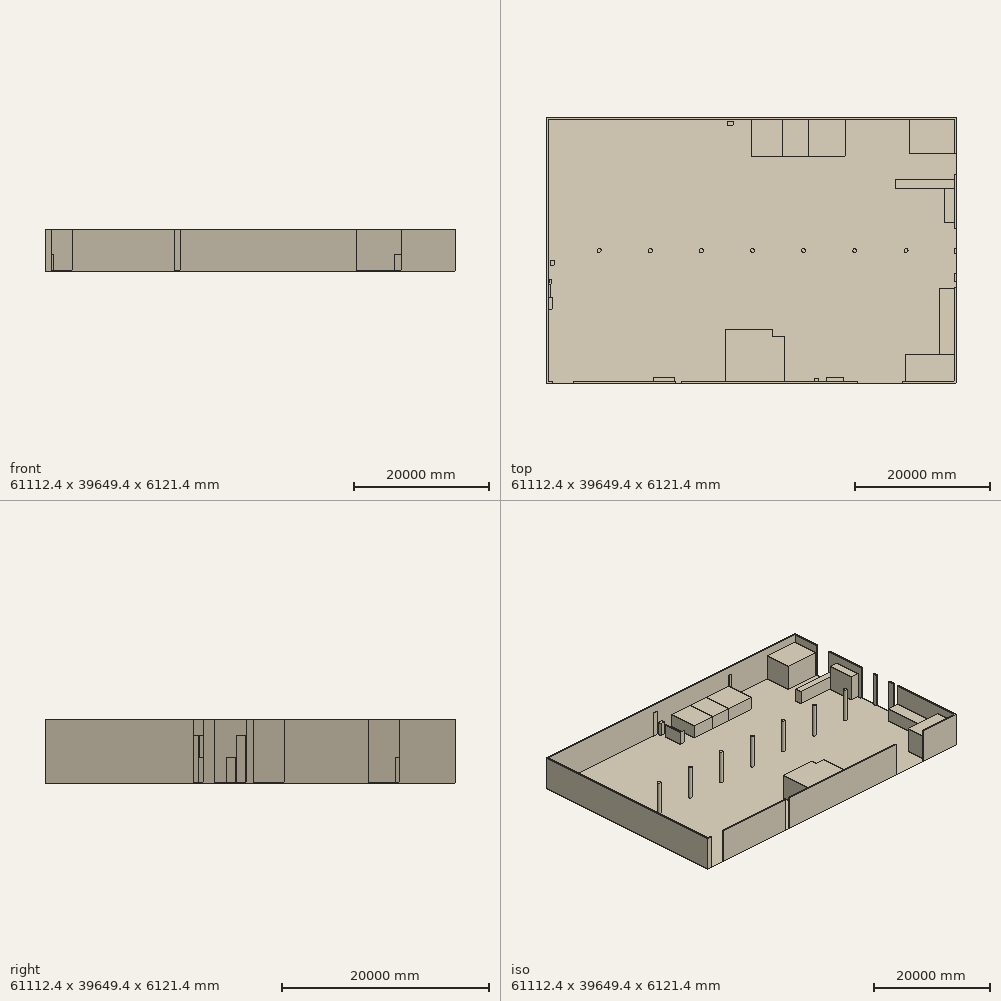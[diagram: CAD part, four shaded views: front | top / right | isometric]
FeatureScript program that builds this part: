
annotation { "Feature Type Name" : "Feature", "Feature Type Description" : "" }
export const myFeature = defineFeature(function(context is Context, id is Id, definition is map)
    precondition{}
    {
        {
            var Q0;
            Q0=qCreatedBy(makeId("Top.planeOp"),FACE);
            var sketch = newSketch(context, id + "F0", { "sketchPlane" : qUnion([Q0])});
            skLineSegment(sketch, "E0.bottom", {"start": v(30556.2, 19824.7) * mm, "end": v(-30556.2, 19824.7) * mm});
            skLineSegment(sketch, "E0.top", {"start": v(30556.2, -19824.7) * mm, "end": v(22479, -19824.7) * mm});
            skLineSegment(sketch, "E0.left", {"start": v(30556.2, 19824.7) * mm, "end": v(30556.2, 14439.9) * mm});
            skLineSegment(sketch, "E0.right", {"start": v(-30556.2, 19824.7) * mm, "end": v(-30556.2, -19824.7) * mm});
            skPoint(sketch, "E0.middle", {"position": v(0, 0) * mm});
            skPoint(sketch, "E1", {"position": v(30556.2, 18148.3) * mm});
            skPoint(sketch, "E2", {"position": v(30556.2, 15100.3) * mm});
            skPoint(sketch, "E3", {"position": v(30556.2, 14439.9) * mm});
            skPoint(sketch, "E4", {"position": v(30556.2, 11391.9) * mm});
            skPoint(sketch, "E5", {"position": v(30556.2, 10731.5) * mm});
            skPoint(sketch, "E6", {"position": v(30556.2, 7683.5) * mm});
            skPoint(sketch, "E7", {"position": v(30556.2, 7023.1) * mm});
            skPoint(sketch, "E8", {"position": v(30556.2, 3975.1) * mm});
            skPoint(sketch, "E9", {"position": v(30556.2, 3314.7) * mm});
            skPoint(sketch, "E10", {"position": v(30556.2, 266.7) * mm});
            skPoint(sketch, "E11", {"position": v(30556.2, -393.7) * mm});
            skPoint(sketch, "E12", {"position": v(30556.2, -3441.7) * mm});
            skPoint(sketch, "E13", {"position": v(30556.2, -4584.7) * mm});
            skPoint(sketch, "E14", {"position": v(30556.2, -5499.1) * mm});
            skPoint(sketch, "E15", {"position": v(-29641.8, -19824.7) * mm});
            skPoint(sketch, "E16", {"position": v(-26593.8, -19824.7) * mm});
            skPoint(sketch, "E17", {"position": v(-11353.8, -19824.7) * mm});
            skPoint(sketch, "E18", {"position": v(-10439.4, -19824.7) * mm});
            skPoint(sketch, "E19", {"position": v(15773.4, -19824.7) * mm});
            skPoint(sketch, "E20", {"position": v(22479, -19824.7) * mm});
            skLineSegment(sketch, "E21.0", {"start": v(30302.2, -19570.7) * mm, "end": v(22479, -19570.7) * mm});
            skLineSegment(sketch, "E21.1", {"start": v(30302.2, 19570.7) * mm, "end": v(30302.2, 14439.9) * mm});
            skLineSegment(sketch, "E21.2", {"start": v(30302.2, 19570.7) * mm, "end": v(-30302.2, 19570.7) * mm});
            skLineSegment(sketch, "E21.3", {"start": v(-30302.2, 19570.7) * mm, "end": v(-30302.2, -19570.7) * mm});
            skLineSegment(sketch, "E22", {"start": v(30556.2, 18148.3) * mm, "end": v(30302.2, 18148.3) * mm});
            skLineSegment(sketch, "E23", {"start": v(30556.2, 15100.3) * mm, "end": v(30302.2, 15100.3) * mm});
            skLineSegment(sketch, "E24", {"start": v(30556.2, 14439.9) * mm, "end": v(30302.2, 14439.9) * mm});
            skLineSegment(sketch, "E25", {"start": v(30556.2, 11391.9) * mm, "end": v(30302.2, 11391.9) * mm});
            skLineSegment(sketch, "E26", {"start": v(30556.2, 10731.5) * mm, "end": v(30302.2, 10731.5) * mm});
            skLineSegment(sketch, "E27", {"start": v(30556.2, 7683.5) * mm, "end": v(30302.2, 7683.5) * mm});
            skLineSegment(sketch, "E28", {"start": v(30556.2, 7023.1) * mm, "end": v(30302.2, 7023.1) * mm});
            skLineSegment(sketch, "E29", {"start": v(30556.2, 3975.1) * mm, "end": v(30302.2, 3975.1) * mm});
            skLineSegment(sketch, "E30", {"start": v(30556.2, 3314.7) * mm, "end": v(30302.2, 3314.7) * mm});
            skLineSegment(sketch, "E31", {"start": v(30556.2, 266.7) * mm, "end": v(30302.2, 266.7) * mm});
            skLineSegment(sketch, "E32", {"start": v(30556.2, -393.7) * mm, "end": v(30302.2, -393.7) * mm});
            skLineSegment(sketch, "E33", {"start": v(30556.2, -3441.7) * mm, "end": v(30302.2, -3441.7) * mm});
            skLineSegment(sketch, "E34", {"start": v(30556.2, -4584.7) * mm, "end": v(30302.2, -4584.7) * mm});
            skLineSegment(sketch, "E35", {"start": v(30556.2, -5499.1) * mm, "end": v(30302.2, -5499.1) * mm});
            skLineSegment(sketch, "E36", {"start": v(22479, -19824.7) * mm, "end": v(22479, -19570.7) * mm});
            skLineSegment(sketch, "E37", {"start": v(15773.4, -19824.7) * mm, "end": v(15773.4, -19570.7) * mm});
            skLineSegment(sketch, "E38", {"start": v(-10439.4, -19824.7) * mm, "end": v(-10439.4, -19570.7) * mm});
            skLineSegment(sketch, "E39", {"start": v(-11353.8, -19824.7) * mm, "end": v(-11353.8, -19570.7) * mm});
            skLineSegment(sketch, "E40", {"start": v(-26593.8, -19824.7) * mm, "end": v(-26593.8, -19570.7) * mm});
            skLineSegment(sketch, "E41", {"start": v(-29641.8, -19824.7) * mm, "end": v(-29641.8, -19570.7) * mm});
            skLineSegment(sketch, "E42.trimOffspring", {"start": v(-29641.8, -19824.7) * mm, "end": v(-30556.2, -19824.7) * mm});
            skLineSegment(sketch, "E43.trimOffspring", {"start": v(-29641.8, -19570.7) * mm, "end": v(-30302.2, -19570.7) * mm});
            skLineSegment(sketch, "E44.trimOffspring", {"start": v(-11353.8, -19824.7) * mm, "end": v(-26593.8, -19824.7) * mm});
            skLineSegment(sketch, "E45.trimOffspring", {"start": v(-11353.8, -19570.7) * mm, "end": v(-26593.8, -19570.7) * mm});
            skLineSegment(sketch, "E46.trimOffspring", {"start": v(15773.4, -19824.7) * mm, "end": v(-10439.4, -19824.7) * mm});
            skLineSegment(sketch, "E47.trimOffspring", {"start": v(15773.4, -19570.7) * mm, "end": v(-10439.4, -19570.7) * mm});
            skLineSegment(sketch, "E48.trimOffspring", {"start": v(30556.2, -5499.1) * mm, "end": v(30556.2, -19824.7) * mm});
            skLineSegment(sketch, "E49.trimOffspring", {"start": v(30302.2, -5499.1) * mm, "end": v(30302.2, -19570.7) * mm});
            skLineSegment(sketch, "E50.trimOffspring", {"start": v(30556.2, -3441.7) * mm, "end": v(30556.2, -4584.7) * mm});
            skLineSegment(sketch, "E51.trimOffspring", {"start": v(30302.2, -3441.7) * mm, "end": v(30302.2, -4584.7) * mm});
            skLineSegment(sketch, "E52.trimOffspring", {"start": v(30556.2, 266.7) * mm, "end": v(30556.2, -393.7) * mm});
            skLineSegment(sketch, "E53.trimOffspring", {"start": v(30302.2, 266.7) * mm, "end": v(30302.2, -393.7) * mm});
            skLineSegment(sketch, "E54.trimOffspring", {"start": v(30556.2, 11391.9) * mm, "end": v(30556.2, 3314.7) * mm});
            skLineSegment(sketch, "E55.trimOffspring", {"start": v(30302.2, 11391.9) * mm, "end": v(30302.2, 3314.7) * mm});
            skLineSegment(sketch, "E56", {"start": v(32965.05, -38.1) * mm, "end": v(-36390.89, -38.1) * mm, "construction": true});
            skPoint(sketch, "E57", {"position": v(23037.8, -38.1) * mm});
            skPoint(sketch, "E58", {"position": v(15417.8, -38.1) * mm});
            skPoint(sketch, "E59", {"position": v(7797.8, -38.1) * mm});
            skPoint(sketch, "E60", {"position": v(177.8, -38.1) * mm});
            skPoint(sketch, "E61", {"position": v(-7442.2, -38.1) * mm});
            skPoint(sketch, "E62", {"position": v(-15062.2, -38.1) * mm});
            skPoint(sketch, "E63", {"position": v(-22682.2, -38.1) * mm});
            skCircle(sketch, "E64", {"center": v(23037.8, -38.1) * mm, "radius": 304.8 * mm});
            skCircle(sketch, "E65", {"center": v(15417.8, -38.1) * mm, "radius": 304.8 * mm});
            skCircle(sketch, "E66", {"center": v(7797.8, -38.1) * mm, "radius": 304.8 * mm});
            skCircle(sketch, "E67", {"center": v(-7442.2, -38.1) * mm, "radius": 304.8 * mm});
            skCircle(sketch, "E68", {"center": v(-15062.2, -38.1) * mm, "radius": 304.8 * mm});
            skCircle(sketch, "E69", {"center": v(-22682.2, -38.1) * mm, "radius": 304.8 * mm});
            skCircle(sketch, "E70", {"center": v(177.8, -38.1) * mm, "radius": 304.8 * mm});
            skSolve(sketch);
        }
        {
            var Q0;
            {var subQ4=sQuery(id+"F0.wireOp",EDGE,"E0.bottom");Q0=makeQuery(id+"F0.imprint","IMPRINT",FACE,{"disambiguationData":[TD([[makeQuery(id+"F0.imprint","IMPRINT",EDGE,{"derivedFrom":subQ4}),1.0]])]});}
            var Q1;
            {var subQ0=sQuery(id+"F0.wireOp",EDGE,"E22");Q1=makeQuery(id+"F0.imprint","IMPRINT",FACE,{"disambiguationData":[TD([[makeQuery(id+"F0.imprint","IMPRINT",EDGE,{"derivedFrom":subQ0}),1.0]])]});}
            var Q2;
            {var subQ2=sQuery(id+"F0.wireOp",EDGE,"E23");Q2=makeQuery(id+"F0.imprint","IMPRINT",FACE,{"disambiguationData":[TD([[makeQuery(id+"F0.imprint","IMPRINT",EDGE,{"derivedFrom":subQ2}),1.0]])]});}
            var Q3;
            {var subQ0=sQuery(id+"F0.wireOp",EDGE,"E25");Q3=makeQuery(id+"F0.imprint","IMPRINT",FACE,{"disambiguationData":[TD([[makeQuery(id+"F0.imprint","IMPRINT",EDGE,{"derivedFrom":subQ0}),1.0]])]});}
            var Q4;
            {var subQ0=sQuery(id+"F0.wireOp",EDGE,"E26");Q4=makeQuery(id+"F0.imprint","IMPRINT",FACE,{"disambiguationData":[TD([[makeQuery(id+"F0.imprint","IMPRINT",EDGE,{"derivedFrom":subQ0}),1.0]])]});}
            var Q5;
            {var subQ0=sQuery(id+"F0.wireOp",EDGE,"E27");Q5=makeQuery(id+"F0.imprint","IMPRINT",FACE,{"disambiguationData":[TD([[makeQuery(id+"F0.imprint","IMPRINT",EDGE,{"derivedFrom":subQ0}),1.0]])]});}
            var Q6;
            {var subQ0=sQuery(id+"F0.wireOp",EDGE,"E28");Q6=makeQuery(id+"F0.imprint","IMPRINT",FACE,{"disambiguationData":[TD([[makeQuery(id+"F0.imprint","IMPRINT",EDGE,{"derivedFrom":subQ0}),1.0]])]});}
            var Q7;
            {var subQ0=sQuery(id+"F0.wireOp",EDGE,"E29");Q7=makeQuery(id+"F0.imprint","IMPRINT",FACE,{"disambiguationData":[TD([[makeQuery(id+"F0.imprint","IMPRINT",EDGE,{"derivedFrom":subQ0}),1.0]])]});}
            var Q8;
            Q8=makeQuery(id+"F0.imprint","IMPRINT",FACE,{"disambiguationData":[TD([[makeQuery(id+"F0.imprint","IMPRINT",EDGE,{"derivedFrom":sQuery(id+"F0.wireOp",EDGE,"E31")}),1.0]])]});
            var Q9;
            Q9=makeQuery(id+"F0.imprint","IMPRINT",FACE,{"disambiguationData":[TD([[makeQuery(id+"F0.imprint","IMPRINT",EDGE,{"derivedFrom":sQuery(id+"F0.wireOp",EDGE,"E33")}),1.0]])]});
            var Q10;
            Q10=makeQuery(id+"F0.imprint","IMPRINT",FACE,{"disambiguationData":[TD([[makeQuery(id+"F0.imprint","IMPRINT",EDGE,{"derivedFrom":sQuery(id+"F0.wireOp",EDGE,"E0.top")}),-1.0]])]});
            var Q11;
            Q11=makeQuery(id+"F0.imprint","IMPRINT",FACE,{"disambiguationData":[TD([[makeQuery(id+"F0.imprint","IMPRINT",EDGE,{"derivedFrom":sQuery(id+"F0.wireOp",EDGE,"E37")}),1.0]])]});
            var Q12;
            Q12=makeQuery(id+"F0.imprint","IMPRINT",FACE,{"disambiguationData":[TD([[makeQuery(id+"F0.imprint","IMPRINT",EDGE,{"derivedFrom":sQuery(id+"F0.wireOp",EDGE,"E39")}),1.0]])]});
            var Q13;
            Q13=makeQuery(id+"F0.imprint","IMPRINT",FACE,{"disambiguationData":[TD([[makeQuery(id+"F0.imprint","IMPRINT",EDGE,{"derivedFrom":sQuery(id+"F0.wireOp",EDGE,"E64")}),1.0]])]});
            var Q14;
            Q14=makeQuery(id+"F0.imprint","IMPRINT",FACE,{"disambiguationData":[TD([[makeQuery(id+"F0.imprint","IMPRINT",EDGE,{"derivedFrom":sQuery(id+"F0.wireOp",EDGE,"E65")}),1.0]])]});
            var Q15;
            Q15=makeQuery(id+"F0.imprint","IMPRINT",FACE,{"disambiguationData":[TD([[makeQuery(id+"F0.imprint","IMPRINT",EDGE,{"derivedFrom":sQuery(id+"F0.wireOp",EDGE,"E66")}),1.0]])]});
            var Q16;
            Q16=makeQuery(id+"F0.imprint","IMPRINT",FACE,{"disambiguationData":[TD([[makeQuery(id+"F0.imprint","IMPRINT",EDGE,{"derivedFrom":sQuery(id+"F0.wireOp",EDGE,"E67")}),1.0]])]});
            var Q17;
            Q17=makeQuery(id+"F0.imprint","IMPRINT",FACE,{"disambiguationData":[TD([[makeQuery(id+"F0.imprint","IMPRINT",EDGE,{"derivedFrom":sQuery(id+"F0.wireOp",EDGE,"E68")}),1.0]])]});
            var Q18;
            Q18=makeQuery(id+"F0.imprint","IMPRINT",FACE,{"disambiguationData":[TD([[makeQuery(id+"F0.imprint","IMPRINT",EDGE,{"derivedFrom":sQuery(id+"F0.wireOp",EDGE,"E69")}),1.0]])]});
            var Q19;
            Q19=makeQuery(id+"F0.imprint","IMPRINT",FACE,{"disambiguationData":[TD([[makeQuery(id+"F0.imprint","IMPRINT",EDGE,{"derivedFrom":sQuery(id+"F0.wireOp",EDGE,"E70")}),1.0]])]});
            extrude(context, id + "F1", {"entities" : qUnion([Q0, Q1, Q2, Q3, Q4, Q5, Q6, Q7, Q8, Q9, Q10, Q11, Q12, Q13, Q14, Q15, Q16, Q17, Q18, Q19]), "depth" : 6096 * mm, "offsetDistance" : 25.4 * mm});
        }
        {
            var Q0;
            Q0=qCreatedBy(makeId("Top.planeOp"),FACE);
            var sketch = newSketch(context, id + "F2", { "sketchPlane" : qUnion([Q0])});
            skLineSegment(sketch, "E71.0.0", {"start": v(30556.2, -5499.1) * mm, "end": v(30302.2, -5499.1) * mm, "construction": true});
            skLineSegment(sketch, "E71.0.1", {"start": v(30302.2, -5499.1) * mm, "end": v(30302.2, -19570.7) * mm, "construction": true});
            skLineSegment(sketch, "E71.0.2", {"start": v(30302.2, -19570.7) * mm, "end": v(22479, -19570.7) * mm, "construction": true});
            skLineSegment(sketch, "E71.0.3", {"start": v(22479, -19570.7) * mm, "end": v(22479, -19824.7) * mm, "construction": true});
            skLineSegment(sketch, "E71.0.4", {"start": v(22479, -19824.7) * mm, "end": v(30556.2, -19824.7) * mm, "construction": true});
            skLineSegment(sketch, "E71.0.5", {"start": v(30556.2, -19824.7) * mm, "end": v(30556.2, -5499.1) * mm, "construction": true});
            skLineSegment(sketch, "E72.0.0", {"start": v(-10439.4, -19570.7) * mm, "end": v(-10439.4, -19824.7) * mm, "construction": true});
            skLineSegment(sketch, "E72.0.1", {"start": v(-10439.4, -19824.7) * mm, "end": v(15773.4, -19824.7) * mm, "construction": true});
            skLineSegment(sketch, "E72.0.2", {"start": v(15773.4, -19824.7) * mm, "end": v(15773.4, -19570.7) * mm, "construction": true});
            skLineSegment(sketch, "E72.0.3", {"start": v(15773.4, -19570.7) * mm, "end": v(-10439.4, -19570.7) * mm, "construction": true});
            skLineSegment(sketch, "E73.0.0", {"start": v(-26593.8, -19570.7) * mm, "end": v(-26593.8, -19824.7) * mm, "construction": true});
            skLineSegment(sketch, "E73.0.1", {"start": v(-26593.8, -19824.7) * mm, "end": v(-11353.8, -19824.7) * mm, "construction": true});
            skLineSegment(sketch, "E73.0.2", {"start": v(-11353.8, -19824.7) * mm, "end": v(-11353.8, -19570.7) * mm, "construction": true});
            skLineSegment(sketch, "E73.0.3", {"start": v(-11353.8, -19570.7) * mm, "end": v(-26593.8, -19570.7) * mm, "construction": true});
            skLineSegment(sketch, "E74.0.0", {"start": v(-30302.2, 19570.7) * mm, "end": v(4546.6, 19570.7) * mm, "construction": true});
            skLineSegment(sketch, "E74.0.1", {"start": v(30302.2, 19570.7) * mm, "end": v(30302.2, 14439.9) * mm, "construction": true});
            skLineSegment(sketch, "E74.0.2", {"start": v(30302.2, 14439.9) * mm, "end": v(30556.2, 14439.9) * mm, "construction": true});
            skLineSegment(sketch, "E74.0.3", {"start": v(30556.2, 14439.9) * mm, "end": v(30556.2, 19824.7) * mm, "construction": true});
            skLineSegment(sketch, "E74.0.4", {"start": v(30556.2, 19824.7) * mm, "end": v(-30556.2, 19824.7) * mm, "construction": true});
            skLineSegment(sketch, "E74.0.5", {"start": v(-30556.2, 19824.7) * mm, "end": v(-30556.2, -19824.7) * mm, "construction": true});
            skLineSegment(sketch, "E74.0.6", {"start": v(-30556.2, -19824.7) * mm, "end": v(-29641.8, -19824.7) * mm, "construction": true});
            skLineSegment(sketch, "E74.0.7", {"start": v(-29641.8, -19824.7) * mm, "end": v(-29641.8, -19570.7) * mm, "construction": true});
            skLineSegment(sketch, "E74.0.8", {"start": v(-29641.8, -19570.7) * mm, "end": v(-30302.2, -19570.7) * mm, "construction": true});
            skLineSegment(sketch, "E74.0.9", {"start": v(-30302.2, -19570.7) * mm, "end": v(-30302.2, 19570.7) * mm, "construction": true});
            skLineSegment(sketch, "E75.0.0", {"start": v(30302.2, 11391.9) * mm, "end": v(30302.2, 3314.7) * mm, "construction": true});
            skLineSegment(sketch, "E75.0.1", {"start": v(30302.2, 3314.7) * mm, "end": v(30556.2, 3314.7) * mm, "construction": true});
            skLineSegment(sketch, "E75.0.2", {"start": v(30556.2, 3314.7) * mm, "end": v(30556.2, 11391.9) * mm, "construction": true});
            skLineSegment(sketch, "E75.0.3", {"start": v(30556.2, 11391.9) * mm, "end": v(30302.2, 11391.9) * mm, "construction": true});
            skLineSegment(sketch, "E76.0.0", {"start": v(30302.2, -393.7) * mm, "end": v(30556.2, -393.7) * mm, "construction": true});
            skLineSegment(sketch, "E76.0.1", {"start": v(30556.2, -393.7) * mm, "end": v(30556.2, 266.7) * mm, "construction": true});
            skLineSegment(sketch, "E76.0.2", {"start": v(30556.2, 266.7) * mm, "end": v(30302.2, 266.7) * mm, "construction": true});
            skLineSegment(sketch, "E76.0.3", {"start": v(30302.2, 266.7) * mm, "end": v(30302.2, -393.7) * mm, "construction": true});
            skLineSegment(sketch, "E77.0.0", {"start": v(30302.2, -4584.7) * mm, "end": v(30556.2, -4584.7) * mm, "construction": true});
            skLineSegment(sketch, "E77.0.1", {"start": v(30556.2, -4584.7) * mm, "end": v(30556.2, -3441.7) * mm, "construction": true});
            skLineSegment(sketch, "E77.0.2", {"start": v(30556.2, -3441.7) * mm, "end": v(30302.2, -3441.7) * mm, "construction": true});
            skLineSegment(sketch, "E77.0.3", {"start": v(30302.2, -3441.7) * mm, "end": v(30302.2, -4584.7) * mm, "construction": true});
            skLineSegment(sketch, "E78.bottom", {"start": v(22987, -19570.7) * mm, "end": v(30302.2, -19570.7) * mm});
            skLineSegment(sketch, "E78.top", {"start": v(22987, -15506.7) * mm, "end": v(28041.6, -15506.7) * mm});
            skLineSegment(sketch, "E78.left", {"start": v(22987, -19570.7) * mm, "end": v(22987, -15506.7) * mm});
            skLineSegment(sketch, "E78.right", {"start": v(30302.2, -19570.7) * mm, "end": v(30302.2, -15506.7) * mm});
            skLineSegment(sketch, "E79.bottom", {"start": v(30302.2, -15506.7) * mm, "end": v(28041.6, -15506.7) * mm});
            skLineSegment(sketch, "E79.top", {"start": v(30302.2, -5600.7) * mm, "end": v(28041.6, -5600.7) * mm});
            skLineSegment(sketch, "E79.left", {"start": v(30302.2, -15506.7) * mm, "end": v(30302.2, -5600.7) * mm});
            skLineSegment(sketch, "E79.right", {"start": v(28041.6, -15506.7) * mm, "end": v(28041.6, -5600.7) * mm});
            skLineSegment(sketch, "E80.bottom", {"start": v(30302.2, 9309.1) * mm, "end": v(21513.8, 9309.1) * mm});
            skLineSegment(sketch, "E80.top", {"start": v(30302.2, 10579.1) * mm, "end": v(21513.8, 10579.1) * mm});
            skLineSegment(sketch, "E80.left", {"start": v(30302.2, 9309.1) * mm, "end": v(30302.2, 10579.1) * mm});
            skLineSegment(sketch, "E80.right", {"start": v(21513.8, 9309.1) * mm, "end": v(21513.8, 10579.1) * mm});
            skLineSegment(sketch, "E81.top", {"start": v(30302.2, 4127.5) * mm, "end": v(28702, 4127.5) * mm});
            skLineSegment(sketch, "E81.left", {"start": v(30302.2, 9309.1) * mm, "end": v(30302.2, 4127.5) * mm});
            skLineSegment(sketch, "E81.right", {"start": v(28702, 9309.1) * mm, "end": v(28702, 4127.5) * mm});
            skLineSegment(sketch, "E82.bottom", {"start": v(30302.2, 14465.3) * mm, "end": v(23520.4, 14465.3) * mm});
            skLineSegment(sketch, "E82.top", {"start": v(30302.2, 19570.7) * mm, "end": v(23520.4, 19570.7) * mm});
            skLineSegment(sketch, "E82.left", {"start": v(30302.2, 14465.3) * mm, "end": v(30302.2, 19570.7) * mm});
            skLineSegment(sketch, "E82.right", {"start": v(23520.4, 14465.3) * mm, "end": v(23520.4, 19570.7) * mm});
            skLineSegment(sketch, "E83.bottom", {"start": v(14541.5, -16675.1) * mm, "end": v(8445.5, -16675.1) * mm});
            skLineSegment(sketch, "E83.top", {"start": v(14541.5, -15252.7) * mm, "end": v(8445.5, -15252.7) * mm});
            skLineSegment(sketch, "E83.left", {"start": v(14541.5, -16675.1) * mm, "end": v(14541.5, -15252.7) * mm});
            skLineSegment(sketch, "E83.right", {"start": v(8445.5, -16675.1) * mm, "end": v(8445.5, -15252.7) * mm});
            skLineSegment(sketch, "E84.bottom", {"start": v(14084.3, -11290.3) * mm, "end": v(15430.5, -11290.3) * mm, "construction": true});
            skLineSegment(sketch, "E84.top", {"start": v(14084.3, -13728.7) * mm, "end": v(15430.5, -13728.7) * mm, "construction": true});
            skLineSegment(sketch, "E84.left", {"start": v(14084.3, -11290.3) * mm, "end": v(14084.3, -13728.7) * mm, "construction": true});
            skLineSegment(sketch, "E84.right", {"start": v(15430.5, -11290.3) * mm, "end": v(15430.5, -13728.7) * mm, "construction": true});
            skLineSegment(sketch, "E85.bottom", {"start": v(17018, -5676.9) * mm, "end": v(15798.8, -5676.9) * mm});
            skLineSegment(sketch, "E85.top", {"start": v(17018, -3136.9) * mm, "end": v(15798.8, -3136.9) * mm});
            skLineSegment(sketch, "E85.left", {"start": v(17018, -5676.9) * mm, "end": v(17018, -3136.9) * mm});
            skLineSegment(sketch, "E86.bottom", {"start": v(17018, -1257.3) * mm, "end": v(15798.8, -1257.3) * mm});
            skLineSegment(sketch, "E86.top", {"start": v(17018, 1282.7) * mm, "end": v(15798.8, 1282.7) * mm});
            skLineSegment(sketch, "E86.left", {"start": v(17018, -1257.3) * mm, "end": v(17018, 1282.7) * mm});
            skLineSegment(sketch, "E87.bottom", {"start": v(17018, 3162.3) * mm, "end": v(15798.8, 3162.3) * mm});
            skLineSegment(sketch, "E87.top", {"start": v(17018, 5702.3) * mm, "end": v(15798.8, 5702.3) * mm});
            skLineSegment(sketch, "E87.left", {"start": v(17018, 3162.3) * mm, "end": v(17018, 5702.3) * mm});
            skLineSegment(sketch, "E87.right", {"start": v(2895.6, 3162.3) * mm, "end": v(2895.6, 5702.3) * mm});
            skLineSegment(sketch, "E88.bottom", {"start": v(17018, 7581.9) * mm, "end": v(15798.8, 7581.9) * mm});
            skLineSegment(sketch, "E88.top", {"start": v(17018, 10121.9) * mm, "end": v(15798.8, 10121.9) * mm});
            skLineSegment(sketch, "E88.left", {"start": v(17018, 7581.9) * mm, "end": v(17018, 10121.9) * mm});
            skLineSegment(sketch, "E89.bottom", {"start": v(-18034, -10198.1) * mm, "end": v(-13055.6, -10198.1) * mm});
            skLineSegment(sketch, "E89.top", {"start": v(-18034, -12331.7) * mm, "end": v(-13055.6, -12331.7) * mm});
            skLineSegment(sketch, "E89.left", {"start": v(-18034, -10198.1) * mm, "end": v(-18034, -12331.7) * mm});
            skLineSegment(sketch, "E89.right", {"start": v(-13055.6, -10198.1) * mm, "end": v(-13055.6, -12331.7) * mm});
            skLineSegment(sketch, "E90.bottom", {"start": v(-26492.2, -19570.7) * mm, "end": v(-15773.4, -19570.7) * mm});
            skLineSegment(sketch, "E90.top", {"start": v(-26492.2, -17970.5) * mm, "end": v(-15773.4, -17970.5) * mm});
            skLineSegment(sketch, "E90.left", {"start": v(-26492.2, -19570.7) * mm, "end": v(-26492.2, -17970.5) * mm});
            skLineSegment(sketch, "E90.right", {"start": v(-15773.4, -19570.7) * mm, "end": v(-15773.4, -17970.5) * mm});
            skLineSegment(sketch, "E91.bottom", {"start": v(-30302.2, -16446.5) * mm, "end": v(-29362.4, -16446.5) * mm});
            skLineSegment(sketch, "E91.top", {"start": v(-30302.2, -10172.7) * mm, "end": v(-29362.4, -10172.7) * mm});
            skLineSegment(sketch, "E91.left", {"start": v(-30302.2, -16446.5) * mm, "end": v(-30302.2, -10172.7) * mm});
            skLineSegment(sketch, "E91.right", {"start": v(-29362.4, -16446.5) * mm, "end": v(-29362.4, -10172.7) * mm});
            skLineSegment(sketch, "E92.bottom", {"start": v(-28676.6, -5803.9) * mm, "end": v(-27432, -5803.9) * mm});
            skLineSegment(sketch, "E92.top", {"start": v(-28676.6, -2146.3) * mm, "end": v(-27432, -2146.3) * mm});
            skLineSegment(sketch, "E92.left", {"start": v(-28676.6, -5803.9) * mm, "end": v(-28676.6, -2146.3) * mm});
            skLineSegment(sketch, "E92.right", {"start": v(-27432, -5803.9) * mm, "end": v(-27432, -2146.3) * mm});
            skLineSegment(sketch, "E93.bottom", {"start": v(-29718, 19570.7) * mm, "end": v(-27889.2, 19570.7) * mm});
            skLineSegment(sketch, "E93.top", {"start": v(-29718, 18986.5) * mm, "end": v(-27889.2, 18986.5) * mm});
            skLineSegment(sketch, "E93.left", {"start": v(-29718, 19570.7) * mm, "end": v(-29718, 18986.5) * mm});
            skLineSegment(sketch, "E93.right", {"start": v(-27889.2, 19570.7) * mm, "end": v(-27889.2, 18986.5) * mm});
            skLineSegment(sketch, "E94.bottom", {"start": v(-30302.2, 17792.7) * mm, "end": v(-29591, 17792.7) * mm});
            skLineSegment(sketch, "E94.top", {"start": v(-30302.2, 8128) * mm, "end": v(-29591, 8128) * mm});
            skLineSegment(sketch, "E94.left", {"start": v(-30302.2, 17792.7) * mm, "end": v(-30302.2, 8128) * mm});
            skLineSegment(sketch, "E94.right", {"start": v(-29591, 17792.7) * mm, "end": v(-29591, 8128) * mm});
            skLineSegment(sketch, "E95.bottom", {"start": v(13970, 19570.7) * mm, "end": v(8458.2, 19570.7) * mm});
            skLineSegment(sketch, "E95.top", {"start": v(13970, 14058.9) * mm, "end": v(8483.6, 14058.9) * mm});
            skLineSegment(sketch, "E95.left", {"start": v(13970, 19570.7) * mm, "end": v(13970, 14058.9) * mm});
            skLineSegment(sketch, "E95.right", {"start": v(8458.2, 19570.7) * mm, "end": v(8458.2, 14058.9) * mm});
            skLineSegment(sketch, "E96.bottom", {"start": v(8458.2, 19570.7) * mm, "end": v(4546.6, 19570.7) * mm});
            skLineSegment(sketch, "E96.top", {"start": v(8458.2, 14058.9) * mm, "end": v(4572, 14058.9) * mm});
            skLineSegment(sketch, "E96.right", {"start": v(4546.6, 19570.7) * mm, "end": v(4546.6, 14058.9) * mm});
            skLineSegment(sketch, "E97.bottom", {"start": v(4546.6, 19570.7) * mm, "end": v(-25.4, 19570.7) * mm});
            skLineSegment(sketch, "E97.top", {"start": v(4546.6, 14058.9) * mm, "end": v(-25.4, 14058.9) * mm});
            skLineSegment(sketch, "E97.right", {"start": v(-25.4, 19570.7) * mm, "end": v(-25.4, 14058.9) * mm});
            skLineSegment(sketch, "E98.bottom", {"start": v(-11531.6, -19570.7) * mm, "end": v(-14579.6, -19570.7) * mm});
            skLineSegment(sketch, "E98.top", {"start": v(-11531.6, -18961.1) * mm, "end": v(-14579.6, -18961.1) * mm});
            skLineSegment(sketch, "E98.left", {"start": v(-11531.6, -19570.7) * mm, "end": v(-11531.6, -18961.1) * mm});
            skLineSegment(sketch, "E98.right", {"start": v(-14579.6, -19570.7) * mm, "end": v(-14579.6, -18961.1) * mm});
            skLineSegment(sketch, "E99.bottom", {"start": v(13690.6, -19570.7) * mm, "end": v(11125.2, -19570.7) * mm});
            skLineSegment(sketch, "E99.top", {"start": v(13690.6, -18961.1) * mm, "end": v(11125.2, -18961.1) * mm});
            skLineSegment(sketch, "E99.left", {"start": v(13690.6, -19570.7) * mm, "end": v(13690.6, -18961.1) * mm});
            skLineSegment(sketch, "E99.right", {"start": v(11125.2, -19570.7) * mm, "end": v(11125.2, -18961.1) * mm});
            skLineSegment(sketch, "E100.bottom", {"start": v(2895.6, 3162.3) * mm, "end": v(609.6, 3162.3) * mm});
            skLineSegment(sketch, "E100.top", {"start": v(2895.6, 5702.3) * mm, "end": v(609.6, 5702.3) * mm});
            skLineSegment(sketch, "E100.right", {"start": v(609.6, 3162.3) * mm, "end": v(609.6, 5702.3) * mm});
            skLineSegment(sketch, "E101.bottom", {"start": v(-30302.2, -6997.7) * mm, "end": v(-29895.8, -6997.7) * mm});
            skLineSegment(sketch, "E101.top", {"start": v(-30302.2, -5067.3) * mm, "end": v(-29895.8, -5067.3) * mm});
            skLineSegment(sketch, "E101.left", {"start": v(-30302.2, -6997.7) * mm, "end": v(-30302.2, -5067.3) * mm});
            skLineSegment(sketch, "E101.right", {"start": v(-29895.8, -6997.7) * mm, "end": v(-29895.8, -5067.3) * mm});
            skLineSegment(sketch, "E102.bottom", {"start": v(2616.2, -5981.7) * mm, "end": v(1397, -5981.7) * mm, "construction": true});
            skLineSegment(sketch, "E102.top", {"start": v(2616.2, -2324.1) * mm, "end": v(1397, -2324.1) * mm, "construction": true});
            skLineSegment(sketch, "E102.left", {"start": v(2616.2, -5981.7) * mm, "end": v(2616.2, -2324.1) * mm, "construction": true});
            skLineSegment(sketch, "E102.right", {"start": v(1397, -5981.7) * mm, "end": v(1397, -2324.1) * mm, "construction": true});
            skLineSegment(sketch, "E103.left", {"start": v(2895.6, 10121.9) * mm, "end": v(2895.6, 10121.9) * mm});
            skLineSegment(sketch, "E104.top", {"start": v(17018, 10934.7) * mm, "end": v(15798.8, 10934.7) * mm});
            skLineSegment(sketch, "E104.left", {"start": v(17018, 10147.3) * mm, "end": v(17018, 10934.7) * mm});
            skLineSegment(sketch, "E104.right", {"start": v(15798.8, 10147.3) * mm, "end": v(15798.8, 10934.7) * mm});
            skLineSegment(sketch, "E105.bottom", {"start": v(-30302.2, -10172.7) * mm, "end": v(-28778.2, -10172.7) * mm});
            skLineSegment(sketch, "E105.top", {"start": v(-30302.2, -9486.9) * mm, "end": v(-28778.2, -9486.9) * mm});
            skLineSegment(sketch, "E105.left", {"start": v(-30302.2, -10172.7) * mm, "end": v(-30302.2, -9486.9) * mm});
            skLineSegment(sketch, "E105.right", {"start": v(-28778.2, -10172.7) * mm, "end": v(-28778.2, -9486.9) * mm});
            skLineSegment(sketch, "E106", {"start": v(-29591, 13220.7) * mm, "end": v(-30302.2, 13220.7) * mm});
            skLineSegment(sketch, "E107.bottom", {"start": v(-26670, 19570.7) * mm, "end": v(-24841.2, 19570.7) * mm});
            skLineSegment(sketch, "E107.top", {"start": v(-26670, 18808.7) * mm, "end": v(-24841.2, 18808.7) * mm});
            skLineSegment(sketch, "E107.left", {"start": v(-26670, 19570.7) * mm, "end": v(-26670, 18808.7) * mm});
            skLineSegment(sketch, "E107.right", {"start": v(-24841.2, 19570.7) * mm, "end": v(-24841.2, 18808.7) * mm});
            skLineSegment(sketch, "E108.bottom", {"start": v(-30302.2, -6997.7) * mm, "end": v(-29641.8, -6997.7) * mm});
            skLineSegment(sketch, "E108.top", {"start": v(-30302.2, -8826.5) * mm, "end": v(-29641.8, -8826.5) * mm});
            skLineSegment(sketch, "E108.left", {"start": v(-30302.2, -6997.7) * mm, "end": v(-30302.2, -8826.5) * mm});
            skLineSegment(sketch, "E108.right", {"start": v(-29641.8, -6997.7) * mm, "end": v(-29641.8, -8826.5) * mm});
            skLineSegment(sketch, "E109.bottom", {"start": v(-30302.2, 6705.6) * mm, "end": v(-27254.2, 6705.6) * mm});
            skLineSegment(sketch, "E109.top", {"start": v(-30302.2, 5562.6) * mm, "end": v(-27254.2, 5562.6) * mm});
            skLineSegment(sketch, "E109.left", {"start": v(-30302.2, 6705.6) * mm, "end": v(-30302.2, 5562.6) * mm});
            skLineSegment(sketch, "E109.right", {"start": v(-27254.2, 6705.6) * mm, "end": v(-27254.2, 5562.6) * mm});
            skLineSegment(sketch, "E110.bottom", {"start": v(-29514.8, 5562.6) * mm, "end": v(-27990.8, 5562.6) * mm});
            skLineSegment(sketch, "E110.top", {"start": v(-29514.8, 5257.8) * mm, "end": v(-27990.8, 5257.8) * mm});
            skLineSegment(sketch, "E110.left", {"start": v(-29514.8, 5562.6) * mm, "end": v(-29514.8, 5257.8) * mm});
            skLineSegment(sketch, "E110.right", {"start": v(-27990.8, 5562.6) * mm, "end": v(-27990.8, 5257.8) * mm});
            skLineSegment(sketch, "E111.bottom", {"start": v(-27889.2, 19265.9) * mm, "end": v(-26670, 19265.9) * mm});
            skLineSegment(sketch, "E111.top", {"start": v(-27889.2, 19570.7) * mm, "end": v(-26670, 19570.7) * mm});
            skLineSegment(sketch, "E111.left", {"start": v(-27889.2, 19265.9) * mm, "end": v(-27889.2, 19570.7) * mm});
            skLineSegment(sketch, "E111.right", {"start": v(-26670, 19265.9) * mm, "end": v(-26670, 19570.7) * mm});
            skLineSegment(sketch, "E112.bottom", {"start": v(9982.2, -19570.7) * mm, "end": v(9321.8, -19570.7) * mm});
            skLineSegment(sketch, "E112.top", {"start": v(9982.2, -19151.6) * mm, "end": v(9321.8, -19151.6) * mm});
            skLineSegment(sketch, "E112.left", {"start": v(9982.2, -19570.7) * mm, "end": v(9982.2, -19151.6) * mm});
            skLineSegment(sketch, "E112.right", {"start": v(9321.8, -19570.7) * mm, "end": v(9321.8, -19151.6) * mm});
            skLineSegment(sketch, "E113.bottom", {"start": v(4940.3, -19570.7) * mm, "end": v(-3816.35, -19570.7) * mm});
            skLineSegment(sketch, "E113.top", {"start": v(3200.4, -11760.2) * mm, "end": v(-3816.35, -11760.2) * mm});
            skLineSegment(sketch, "E113.left", {"start": v(4940.3, -19570.7) * mm, "end": v(4940.3, -12776.2) * mm});
            skLineSegment(sketch, "E113.right", {"start": v(-3816.35, -19570.7) * mm, "end": v(-3816.35, -11760.2) * mm});
            skLineSegment(sketch, "E114.top", {"start": v(4940.3, -12776.2) * mm, "end": v(3200.4, -12776.2) * mm});
            skLineSegment(sketch, "E114.right", {"start": v(3200.4, -11760.2) * mm, "end": v(3200.4, -12776.2) * mm});
            skLineSegment(sketch, "E115", {"start": v(6121.4, -5676.9) * mm, "end": v(6121.4, -3136.9) * mm});
            skLineSegment(sketch, "E116.trimOffspring", {"start": v(6121.4, -1257.3) * mm, "end": v(6121.4, 1282.7) * mm});
            skLineSegment(sketch, "E117.right", {"start": v(-4832.35, -12420.6) * mm, "end": v(-4832.35, -18605.5) * mm});
            skLineSegment(sketch, "E118.bottom", {"start": v(-4832.35, -18605.5) * mm, "end": v(-10420.35, -18605.5) * mm});
            skLineSegment(sketch, "E118.top", {"start": v(-4832.35, -19570.7) * mm, "end": v(-10420.35, -19570.7) * mm});
            skLineSegment(sketch, "E118.left", {"start": v(-4832.35, -18605.5) * mm, "end": v(-4832.35, -19570.7) * mm});
            skLineSegment(sketch, "E118.right", {"start": v(-10420.35, -18605.5) * mm, "end": v(-10420.35, -19570.7) * mm});
            skLineSegment(sketch, "E119", {"start": v(-4832.35, -12420.6) * mm, "end": v(-3867.15, -12420.6) * mm});
            skLineSegment(sketch, "E120", {"start": v(-3867.15, -12420.6) * mm, "end": v(-3867.15, -18605.5) * mm});
            skLineSegment(sketch, "E121", {"start": v(-3867.15, -18605.5) * mm, "end": v(-4832.35, -18605.5) * mm});
            skLineSegment(sketch, "E122", {"start": v(8483.6, 19570.7) * mm, "end": v(8483.6, 14058.9) * mm});
            skLineSegment(sketch, "E123", {"start": v(4572, 19570.7) * mm, "end": v(4572, 14058.9) * mm});
            skLineSegment(sketch, "E124.trimOffspring", {"start": v(8483.6, 19570.7) * mm, "end": v(13970, 19570.7) * mm, "construction": true});
            skLineSegment(sketch, "E125.trimOffspring", {"start": v(4572, 19570.7) * mm, "end": v(8458.2, 19570.7) * mm, "construction": true});
            skLineSegment(sketch, "E126", {"start": v(2895.6, 7581.9) * mm, "end": v(1651, 7581.9) * mm});
            skLineSegment(sketch, "E127", {"start": v(1651, 7581.9) * mm, "end": v(1651, 8216.9) * mm});
            skLineSegment(sketch, "E128", {"start": v(1651, 8216.9) * mm, "end": v(2895.6, 8216.9) * mm});
            skLineSegment(sketch, "E129", {"start": v(2895.6, 8242.3) * mm, "end": v(2895.6, 10096.5) * mm});
            skLineSegment(sketch, "E130", {"start": v(2895.6, 10121.9) * mm, "end": v(2184.4, 10121.9) * mm});
            skLineSegment(sketch, "E131", {"start": v(2184.4, 10096.5) * mm, "end": v(2184.4, 8242.3) * mm});
            skLineSegment(sketch, "E132", {"start": v(2895.6, 10121.9) * mm, "end": v(2895.6, 11137.9) * mm});
            skLineSegment(sketch, "E133", {"start": v(2895.6, 11137.9) * mm, "end": v(1879.6, 11137.9) * mm});
            skLineSegment(sketch, "E134", {"start": v(1854.2, 11137.9) * mm, "end": v(1854.2, 10121.9) * mm});
            skLineSegment(sketch, "E135", {"start": v(1879.6, 10121.9) * mm, "end": v(2895.6, 10121.9) * mm});
            skLineSegment(sketch, "E136", {"start": v(1854.2, 11137.9) * mm, "end": v(838.2, 11137.9) * mm});
            skLineSegment(sketch, "E137", {"start": v(838.2, 11137.9) * mm, "end": v(838.2, 10121.9) * mm});
            skLineSegment(sketch, "E138", {"start": v(838.2, 10121.9) * mm, "end": v(1854.2, 10121.9) * mm});
            skLineSegment(sketch, "E139", {"start": v(15798.8, 10121.9) * mm, "end": v(15798.8, 7581.9) * mm});
            skLineSegment(sketch, "E140", {"start": v(15798.8, 10121.9) * mm, "end": v(15798.8, 10121.9) * mm});
            skLineSegment(sketch, "E141", {"start": v(15773.4, 9512.3) * mm, "end": v(2921, 9512.3) * mm});
            skLineSegment(sketch, "E142", {"start": v(15798.8, 5702.3) * mm, "end": v(15798.8, 3162.3) * mm});
            skLineSegment(sketch, "E143", {"start": v(15798.8, 1282.7) * mm, "end": v(15798.8, -1257.3) * mm});
            skLineSegment(sketch, "E144", {"start": v(15798.8, -3136.9) * mm, "end": v(15798.8, -5676.9) * mm});
            skLineSegment(sketch, "E145", {"start": v(1879.6, 11137.9) * mm, "end": v(1879.6, 10121.9) * mm});
            skLineSegment(sketch, "E146", {"start": v(2184.4, 10096.5) * mm, "end": v(2895.6, 10096.5) * mm});
            skLineSegment(sketch, "E147", {"start": v(2184.4, 8242.3) * mm, "end": v(2895.6, 8242.3) * mm});
            skLineSegment(sketch, "E148", {"start": v(2921, 9512.3) * mm, "end": v(2921, 7581.9) * mm});
            skLineSegment(sketch, "E149.trimOffspring", {"start": v(2895.6, 10096.5) * mm, "end": v(2895.6, 8242.3) * mm});
            skLineSegment(sketch, "E150.trimOffspring", {"start": v(2895.6, 8216.9) * mm, "end": v(2895.6, 7581.9) * mm});
            skLineSegment(sketch, "E151", {"start": v(15773.4, 9512.3) * mm, "end": v(15773.4, 7581.9) * mm});
            skLineSegment(sketch, "E152", {"start": v(15773.4, 5702.3) * mm, "end": v(15773.4, 3162.3) * mm});
            skLineSegment(sketch, "E153", {"start": v(15773.4, 1282.7) * mm, "end": v(15773.4, -1257.3) * mm});
            skLineSegment(sketch, "E154", {"start": v(15773.4, -3136.9) * mm, "end": v(15773.4, -5676.9) * mm});
            skLineSegment(sketch, "E155.trimOffspring", {"start": v(15773.4, -5676.9) * mm, "end": v(6121.4, -5676.9) * mm});
            skLineSegment(sketch, "E156.trimOffspring", {"start": v(15773.4, -3136.9) * mm, "end": v(6121.4, -3136.9) * mm});
            skLineSegment(sketch, "E157.trimOffspring", {"start": v(15773.4, -1257.3) * mm, "end": v(6121.4, -1257.3) * mm});
            skLineSegment(sketch, "E158.trimOffspring", {"start": v(15773.4, 1282.7) * mm, "end": v(6121.4, 1282.7) * mm});
            skLineSegment(sketch, "E159.trimOffspring", {"start": v(15773.4, 3162.3) * mm, "end": v(2895.6, 3162.3) * mm});
            skLineSegment(sketch, "E160.trimOffspring", {"start": v(15773.4, 5702.3) * mm, "end": v(2895.6, 5702.3) * mm});
            skLineSegment(sketch, "E161.trimOffspring", {"start": v(15773.4, 7581.9) * mm, "end": v(2921, 7581.9) * mm});
            skLineSegment(sketch, "E162", {"start": v(15798.8, 10147.3) * mm, "end": v(17018, 10147.3) * mm});
            skLineSegment(sketch, "E163.bottom", {"start": v(-812.8, 19024.6) * mm, "end": v(-127, 19024.6) * mm});
            skLineSegment(sketch, "E163.top", {"start": v(-812.8, 16560.8) * mm, "end": v(-127, 16560.8) * mm});
            skLineSegment(sketch, "E163.left", {"start": v(-812.8, 19024.6) * mm, "end": v(-812.8, 16560.8) * mm});
            skLineSegment(sketch, "E163.right", {"start": v(-127, 19024.6) * mm, "end": v(-127, 16560.8) * mm});
            skLineSegment(sketch, "E164.bottom", {"start": v(-977.9, 16535.4) * mm, "end": v(-127, 16535.4) * mm});
            skLineSegment(sketch, "E164.top", {"start": v(-977.9, 15011.4) * mm, "end": v(-127, 15011.4) * mm});
            skLineSegment(sketch, "E164.left", {"start": v(-977.9, 16535.4) * mm, "end": v(-977.9, 15011.4) * mm});
            skLineSegment(sketch, "E164.right", {"start": v(-127, 16535.4) * mm, "end": v(-127, 15011.4) * mm});
            skLineSegment(sketch, "E165.bottom", {"start": v(-3263.9, 17805.4) * mm, "end": v(-3225.8, 17805.4) * mm});
            skLineSegment(sketch, "E165.left", {"start": v(-3263.9, 17805.4) * mm, "end": v(-3263.9, 14147.8) * mm});
            skLineSegment(sketch, "E165.right", {"start": v(-3225.8, 17805.4) * mm, "end": v(-3225.8, 14185.9) * mm});
            skLineSegment(sketch, "E166", {"start": v(-2393.95, 14147.8) * mm, "end": v(-2393.95, 14185.9) * mm});
            skLineSegment(sketch, "E167", {"start": v(-2393.95, 14185.9) * mm, "end": v(-3225.8, 14185.9) * mm});
            skLineSegment(sketch, "E168", {"start": v(-3263.9, 14147.8) * mm, "end": v(-2393.95, 14147.8) * mm});
            skLineSegment(sketch, "E169.bottom", {"start": v(-3517.9, 19227.8) * mm, "end": v(-2717.8, 19227.8) * mm});
            skLineSegment(sketch, "E169.top", {"start": v(-3517.9, 18669) * mm, "end": v(-2717.8, 18669) * mm});
            skLineSegment(sketch, "E169.left", {"start": v(-3517.9, 19227.8) * mm, "end": v(-3517.9, 18669) * mm});
            skLineSegment(sketch, "E169.right", {"start": v(-2717.8, 19227.8) * mm, "end": v(-2717.8, 18669) * mm});
            skLineSegment(sketch, "E170.bottom", {"start": v(-3733.8, 19570.7) * mm, "end": v(-4559.3, 19570.7) * mm});
            skLineSegment(sketch, "E170.top", {"start": v(-3733.8, 19469.1) * mm, "end": v(-4559.3, 19469.1) * mm});
            skLineSegment(sketch, "E170.left", {"start": v(-3733.8, 19570.7) * mm, "end": v(-3733.8, 19469.1) * mm});
            skLineSegment(sketch, "E170.right", {"start": v(-4559.3, 19570.7) * mm, "end": v(-4559.3, 19469.1) * mm});
            skLineSegment(sketch, "E171.bottom", {"start": v(13970, 19570.7) * mm, "end": v(14490.7, 19570.7) * mm});
            skLineSegment(sketch, "E171.top", {"start": v(13982.7, 19469.1) * mm, "end": v(14490.7, 19469.1) * mm});
            skLineSegment(sketch, "E171.right", {"start": v(14490.7, 19570.7) * mm, "end": v(14490.7, 19469.1) * mm});
            skLineSegment(sketch, "E172", {"start": v(13982.7, 19469.1) * mm, "end": v(13982.7, 19570.7) * mm});
            skLineSegment(sketch, "E173.trimOffspring", {"start": v(13982.7, 19570.7) * mm, "end": v(30302.2, 19570.7) * mm, "construction": true});
            skLineSegment(sketch, "E174.bottom", {"start": v(-30302.2, -5041.9) * mm, "end": v(-29857.7, -5041.9) * mm});
            skLineSegment(sketch, "E174.top", {"start": v(-30302.2, -4381.5) * mm, "end": v(-29857.7, -4381.5) * mm});
            skLineSegment(sketch, "E174.left", {"start": v(-30302.2, -5041.9) * mm, "end": v(-30302.2, -4381.5) * mm});
            skLineSegment(sketch, "E174.right", {"start": v(-29857.7, -5041.9) * mm, "end": v(-29857.7, -4381.5) * mm});
            skLineSegment(sketch, "E175.bottom", {"start": v(-30302.2, -4965.7) * mm, "end": v(-30143.45, -4965.7) * mm});
            skLineSegment(sketch, "E175.top", {"start": v(-30302.2, -4419.6) * mm, "end": v(-30143.45, -4419.6) * mm});
            skLineSegment(sketch, "E175.left", {"start": v(-30302.2, -4965.7) * mm, "end": v(-30302.2, -4419.6) * mm});
            skLineSegment(sketch, "E175.right", {"start": v(-30143.45, -4965.7) * mm, "end": v(-30143.45, -4419.6) * mm});
            skLineSegment(sketch, "E176.bottom", {"start": v(-30302.2, -4127.5) * mm, "end": v(-30200.6, -4127.5) * mm});
            skLineSegment(sketch, "E176.top", {"start": v(-30302.2, -3733.8) * mm, "end": v(-30200.6, -3733.8) * mm});
            skLineSegment(sketch, "E176.left", {"start": v(-30302.2, -4127.5) * mm, "end": v(-30302.2, -3733.8) * mm});
            skLineSegment(sketch, "E176.right", {"start": v(-30200.6, -4127.5) * mm, "end": v(-30200.6, -3733.8) * mm});
            skLineSegment(sketch, "E177.bottom", {"start": v(-29959.3, -2298.7) * mm, "end": v(-29400.5, -2298.7) * mm});
            skLineSegment(sketch, "E177.top", {"start": v(-29959.3, -1498.6) * mm, "end": v(-29400.5, -1498.6) * mm});
            skLineSegment(sketch, "E177.left", {"start": v(-29959.3, -2298.7) * mm, "end": v(-29959.3, -1498.6) * mm});
            skLineSegment(sketch, "E177.right", {"start": v(-29400.5, -2298.7) * mm, "end": v(-29400.5, -1498.6) * mm});
            skLineSegment(sketch, "E178.bottom", {"start": v(-30302.2, -1333.5) * mm, "end": v(-30200.6, -1333.5) * mm});
            skLineSegment(sketch, "E178.top", {"start": v(-30302.2, -520.7) * mm, "end": v(-30200.6, -520.7) * mm});
            skLineSegment(sketch, "E178.left", {"start": v(-30302.2, -1333.5) * mm, "end": v(-30302.2, -520.7) * mm});
            skLineSegment(sketch, "E178.right", {"start": v(-30200.6, -1333.5) * mm, "end": v(-30200.6, -520.7) * mm});
            skLineSegment(sketch, "E179.bottom", {"start": v(-3213.1, 17805.4) * mm, "end": v(-2882.9, 17805.4) * mm});
            skLineSegment(sketch, "E179.top", {"start": v(-3213.1, 16586.2) * mm, "end": v(-2882.9, 16586.2) * mm});
            skLineSegment(sketch, "E179.left", {"start": v(-3213.1, 17805.4) * mm, "end": v(-3213.1, 16586.2) * mm});
            skLineSegment(sketch, "E179.right", {"start": v(-2882.9, 17805.4) * mm, "end": v(-2882.9, 16586.2) * mm});
            skSolve(sketch);
        }
        {
            var Q0;
            Q0=makeQuery(id+"F2.imprint","IMPRINT",FACE,{"disambiguationData":[TD([[makeQuery(id+"F2.imprint","IMPRINT",EDGE,{"derivedFrom":sQuery(id+"F2.wireOp",EDGE,"E101.top")}),-1.0]])]});
            var Q1;
            Q1=makeQuery(id+"F2.imprint","IMPRINT",FACE,{"disambiguationData":[TD([[makeQuery(id+"F2.imprint","IMPRINT",EDGE,{"derivedFrom":sQuery(id+"F2.wireOp",EDGE,"E98.bottom")}),-1.0]])]});
            var Q2;
            Q2=makeQuery(id+"F2.imprint","IMPRINT",FACE,{"disambiguationData":[TD([[makeQuery(id+"F2.imprint","IMPRINT",EDGE,{"derivedFrom":sQuery(id+"F2.wireOp",EDGE,"E99.bottom")}),-1.0]])]});
            var Q3;
            Q3=makeQuery(id+"F2.imprint","IMPRINT",FACE,{"disambiguationData":[TD([[makeQuery(id+"F2.imprint","IMPRINT",EDGE,{"derivedFrom":sQuery(id+"F2.wireOp",EDGE,"E84.bottom")}),-1.0]])]});
            var Q4;
            Q4=makeQuery(id+"F2.imprint","IMPRINT",FACE,{"disambiguationData":[TD([[makeQuery(id+"F2.imprint","IMPRINT",EDGE,{"derivedFrom":sQuery(id+"F2.wireOp",EDGE,"E78.bottom")}),1.0]])]});
            var Q5;
            Q5=makeQuery(id+"F2.imprint","IMPRINT",FACE,{"disambiguationData":[TD([[makeQuery(id+"F2.imprint","IMPRINT",EDGE,{"derivedFrom":sQuery(id+"F2.wireOp",EDGE,"E102.bottom")}),-1.0]])]});
            var Q6;
            Q6=makeQuery(id+"F2.imprint","IMPRINT",FACE,{"disambiguationData":[TD([[makeQuery(id+"F2.imprint","IMPRINT",EDGE,{"derivedFrom":sQuery(id+"F2.wireOp",EDGE,"E81.top")}),-1.0]])]});
            var Q7;
            Q7=makeQuery(id+"F2.imprint","IMPRINT",FACE,{"disambiguationData":[TD([[makeQuery(id+"F2.imprint","IMPRINT",EDGE,{"derivedFrom":sQuery(id+"F2.wireOp",EDGE,"E82.bottom")}),-1.0]])]});
            var Q8;
            Q8=makeQuery(id+"F2.imprint","IMPRINT",FACE,{"disambiguationData":[TD([[makeQuery(id+"F2.imprint","IMPRINT",EDGE,{"derivedFrom":sQuery(id+"F2.wireOp",EDGE,"E113.bottom")}),-1.0]])]});
            var Q9;
            Q9=makeQuery(id+"F2.imprint","IMPRINT",FACE,{"disambiguationData":[TD([[makeQuery(id+"F2.imprint","IMPRINT",EDGE,{"derivedFrom":sQuery(id+"F2.wireOp",EDGE,"E171.top")}),1.0]])]});
            var Q10;
            Q10=makeQuery(id+"F2.imprint","IMPRINT",FACE,{"disambiguationData":[TD([[makeQuery(id+"F2.imprint","IMPRINT",EDGE,{"derivedFrom":sQuery(id+"F2.wireOp",EDGE,"E170.bottom")}),1.0]])]});
            var Q11;
            Q11=makeQuery(id+"F2.imprint","IMPRINT",FACE,{"disambiguationData":[TD([[makeQuery(id+"F2.imprint","IMPRINT",EDGE,{"derivedFrom":sQuery(id+"F2.wireOp",EDGE,"E175.bottom")}),1.0]])]});
            var Q12;
            Q12=makeQuery(id+"F2.imprint","IMPRINT",FACE,{"disambiguationData":[TD([[makeQuery(id+"F2.imprint","IMPRINT",EDGE,{"derivedFrom":sQuery(id+"F2.wireOp",EDGE,"E176.bottom")}),1.0]])]});
            var Q13;
            Q13=makeQuery(id+"F2.imprint","IMPRINT",FACE,{"disambiguationData":[TD([[makeQuery(id+"F2.imprint","IMPRINT",EDGE,{"derivedFrom":sQuery(id+"F2.wireOp",EDGE,"E178.bottom")}),1.0]])]});
            extrude(context, id + "F3", {"entities" : qUnion([Q0, Q1, Q2, Q3, Q4, Q5, Q6, Q7, Q8, Q9, Q10, Q11, Q12, Q13]), "flatOperationType" : FlatOperationType.REMOVE, "depth" : 4572 * mm, "offsetDistance" : 25.4 * mm, "domain" : OperationDomain.MODEL});
        }
        {
            var Q0;
            Q0=makeQuery(id+"F2.imprint","IMPRINT",FACE,{"disambiguationData":[TD([[makeQuery(id+"F2.imprint","IMPRINT",EDGE,{"derivedFrom":sQuery(id+"F2.wireOp",EDGE,"E108.top")}),1.0]])]});
            var Q1;
            Q1=makeQuery(id+"F2.imprint","IMPRINT",FACE,{"disambiguationData":[TD([[makeQuery(id+"F2.imprint","IMPRINT",EDGE,{"derivedFrom":sQuery(id+"F2.wireOp",EDGE,"E96.bottom")}),1.0]])]});
            var Q2;
            Q2=makeQuery(id+"F2.imprint","IMPRINT",FACE,{"disambiguationData":[TD([[makeQuery(id+"F2.imprint","IMPRINT",EDGE,{"derivedFrom":sQuery(id+"F2.wireOp",EDGE,"E88.top")}),-1.0]])]});
            var Q3;
            Q3=makeQuery(id+"F2.imprint","IMPRINT",FACE,{"disambiguationData":[TD([[makeQuery(id+"F2.imprint","IMPRINT",EDGE,{"derivedFrom":sQuery(id+"F2.wireOp",EDGE,"E103.bottom")}),1.0]])]});
            var Q4;
            Q4=makeQuery(id+"F2.imprint","IMPRINT",FACE,{"disambiguationData":[TD([[makeQuery(id+"F2.imprint","IMPRINT",EDGE,{"derivedFrom":sQuery(id+"F2.wireOp",EDGE,"E80.top")}),1.0]])]});
            var Q5;
            Q5=makeQuery(id+"F2.imprint","IMPRINT",FACE,{"disambiguationData":[TD([[makeQuery(id+"F2.imprint","IMPRINT",EDGE,{"derivedFrom":sQuery(id+"F2.wireOp",EDGE,"RZzpUL3J-bDm2-hje9-ZRdF-o6WNzDrT3lMB.bottom")}),1.0]])]});
            var Q6;
            Q6=makeQuery(id+"F2.imprint","IMPRINT",FACE,{"disambiguationData":[TD([[makeQuery(id+"F2.imprint","IMPRINT",EDGE,{"derivedFrom":sQuery(id+"F2.wireOp",EDGE,"deG2DQC9-hYrt-SXXY-SVAO-WSBKtexY8Rs3.bottom")}),-1.0]])]});
            var Q7;
            Q7=makeQuery(id+"F2.imprint","IMPRINT",FACE,{"disambiguationData":[TD([[makeQuery(id+"F2.imprint","IMPRINT",EDGE,{"derivedFrom":sQuery(id+"F2.wireOp",EDGE,"E79.bottom")}),-1.0]])]});
            var Q8;
            Q8=makeQuery(id+"F7.imprint","IMPRINT",FACE,{"disambiguationData":[TD([[makeQuery(id+"F7.imprint","IMPRINT",EDGE,{"derivedFrom":sQuery(id+"F7.wireOp",EDGE,"PKS6GW7b-xBBg-DLFe-Cp2w-VF4NfTfaE2xo.bottom")}),1.0]])]});
            var Q9;
            Q9=makeQuery(id+"F2.imprint","IMPRINT",FACE,{"disambiguationData":[TD([[makeQuery(id+"F2.imprint","IMPRINT",EDGE,{"derivedFrom":sQuery(id+"F2.wireOp",EDGE,"E95.bottom")}),1.0]])]});
            var Q10;
            Q10=makeQuery(id+"F2.imprint","IMPRINT",FACE,{"disambiguationData":[TD([[makeQuery(id+"F2.imprint","IMPRINT",EDGE,{"derivedFrom":sQuery(id+"F2.wireOp",EDGE,"E97.bottom")}),1.0]])]});
            var Q11;
            {var subQ3=sQuery(id+"F2.wireOp",EDGE,"E103.left");Q11=makeQuery(id+"F2.imprint","IMPRINT",FACE,{"disambiguationData":[TD([[makeQuery(id+"F2.imprint","IMPRINT",EDGE,{"derivedFrom":subQ3}),-1.0]])]});}
            var Q12;
            Q12=makeQuery(id+"F2.imprint","IMPRINT",FACE,{"disambiguationData":[TD([[makeQuery(id+"F2.imprint","IMPRINT",EDGE,{"derivedFrom":sQuery(id+"F2.wireOp",EDGE,"E165.bottom")}),-1.0]])]});
            var Q13;
            Q13=makeQuery(id+"F7.imprint","IMPRINT",FACE,{"disambiguationData":[TD([[makeQuery(id+"F7.imprint","IMPRINT",EDGE,{"derivedFrom":sQuery(id+"F7.wireOp",EDGE,"PKS6GW7b-xBBg-DLFe-Cp2w-VF4NfTfaE2xo.bottom")}),1.0]])]});
            var Q14;
            Q14=makeQuery(id+"F2.imprint","IMPRINT",FACE,{"disambiguationData":[TD([[makeQuery(id+"F2.imprint","IMPRINT",EDGE,{"derivedFrom":sQuery(id+"F2.wireOp",EDGE,"E169.bottom")}),-1.0]])]});
            var Q15;
            Q15=makeQuery(id+"F2.imprint","IMPRINT",FACE,{"disambiguationData":[TD([[makeQuery(id+"F2.imprint","IMPRINT",EDGE,{"derivedFrom":sQuery(id+"F2.wireOp",EDGE,"E112.bottom")}),-1.0]])]});
            var Q16;
            {var subQ4=sQuery(id+"F2.wireOp",EDGE,"E174.bottom");Q16=makeQuery(id+"F2.imprint","IMPRINT",FACE,{"disambiguationData":[TD([[makeQuery(id+"F2.imprint","IMPRINT",EDGE,{"derivedFrom":subQ4}),1.0]])]});}
            var Q17;
            Q17=makeQuery(id+"F2.imprint","IMPRINT",FACE,{"disambiguationData":[TD([[makeQuery(id+"F2.imprint","IMPRINT",EDGE,{"derivedFrom":sQuery(id+"F2.wireOp",EDGE,"E177.bottom")}),1.0]])]});
            extrude(context, id + "F4", {"entities" : qUnion([Q0, Q1, Q2, Q3, Q4, Q5, Q6, Q7, Q8, Q9, Q10, Q11, Q12, Q13, Q14, Q15, Q16, Q17]), "flatOperationType" : FlatOperationType.REMOVE, "depth" : 2438.4 * mm, "offsetDistance" : 25.4 * mm, "domain" : OperationDomain.MODEL});
        }
        {
            var Q0;
            Q0=qCreatedBy(makeId("Top.planeOp"),FACE);
            var sketch = newSketch(context, id + "F5", { "sketchPlane" : qUnion([Q0])});
            skPoint(sketch, "E180.0", {"position": v(-30556.2, 19824.7) * mm});
            skPoint(sketch, "E181.0", {"position": v(30556.2, 19824.7) * mm});
            skPoint(sketch, "E182.0", {"position": v(30556.2, -19824.7) * mm});
            skPoint(sketch, "E183.0", {"position": v(-30556.2, -19824.7) * mm});
            skLineSegment(sketch, "E184.bottom", {"start": v(-30556.2, -19824.7) * mm, "end": v(30556.2, -19824.7) * mm});
            skLineSegment(sketch, "E184.top", {"start": v(-30556.2, 19824.7) * mm, "end": v(30556.2, 19824.7) * mm});
            skLineSegment(sketch, "E184.left", {"start": v(-30556.2, -19824.7) * mm, "end": v(-30556.2, 19824.7) * mm});
            skLineSegment(sketch, "E184.right", {"start": v(30556.2, -19824.7) * mm, "end": v(30556.2, 19824.7) * mm});
            skSolve(sketch);
        }
        {
            var Q0;
            Q0 = qSketchRegion(id + "F5", true);
            extrude(context, id + "F6", {"entities" : qUnion([Q0]), "operationType" : NewBodyOperationType.ADD, "oppositeDirection" : true, "depth" : 25.4 * mm, "offsetDistance" : 25.4 * mm});
        }
    });
